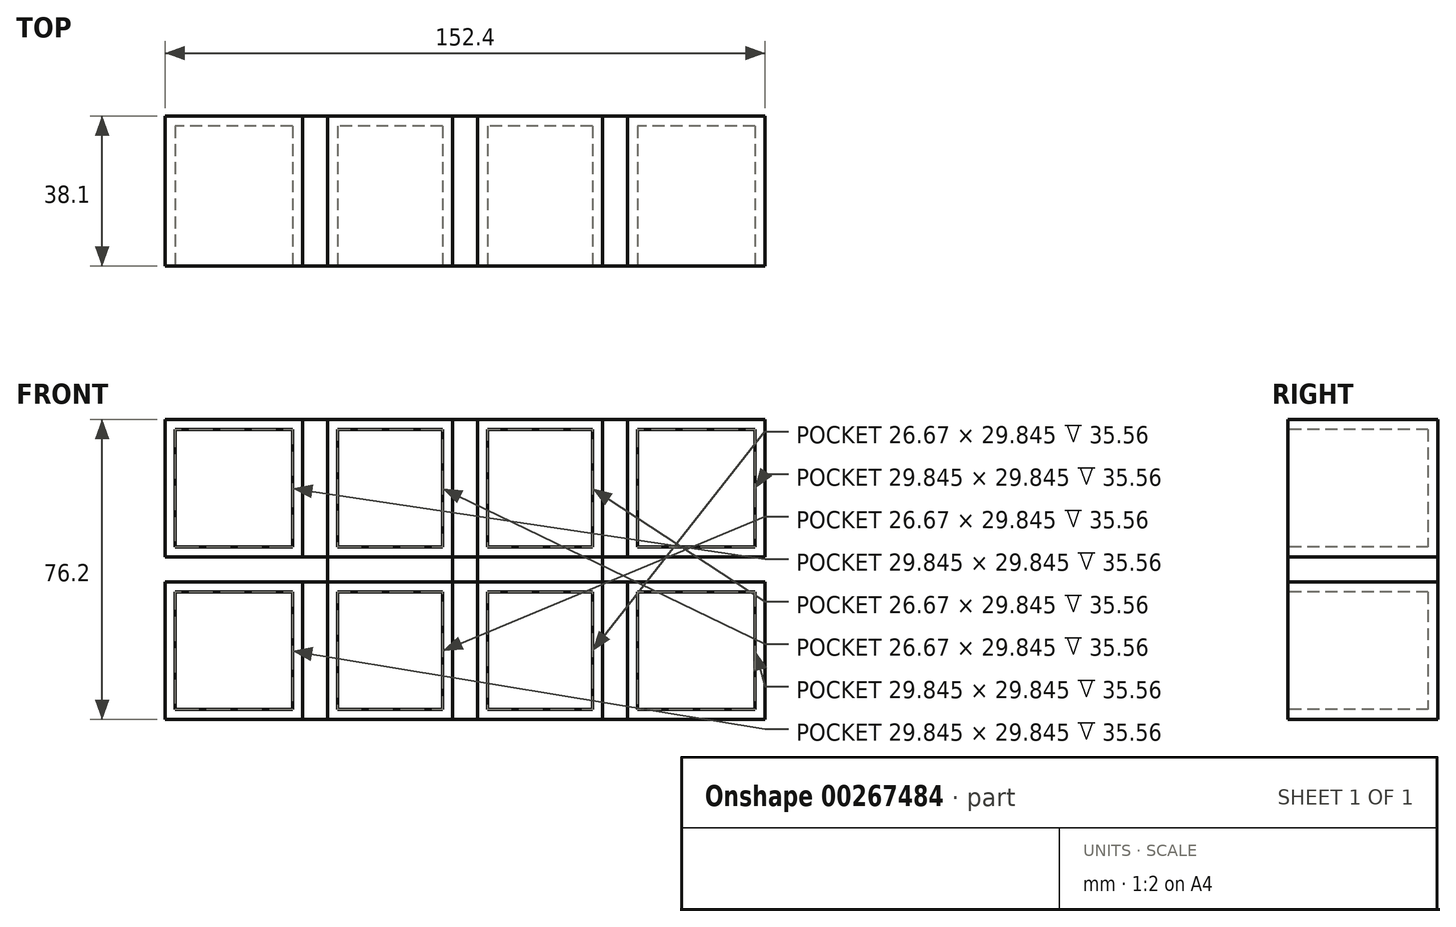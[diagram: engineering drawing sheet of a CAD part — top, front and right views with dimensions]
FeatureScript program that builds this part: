
annotation { "Feature Type Name" : "Feature", "Feature Type Description" : "" }
export const myFeature = defineFeature(function(context is Context, id is Id, definition is map)
    precondition{}
    {
        {
            var Q0;
            Q0=qCreatedBy(makeId("Front.planeOp"),FACE);
            var sketch = newSketch(context, id + "F0", { "sketchPlane" : qUnion([Q0])});
            skLineSegment(sketch, "E0.bottom", {"start": v(76.2, 38.1) * mm, "end": v(-76.2, 38.1) * mm});
            skLineSegment(sketch, "E0.top", {"start": v(76.2, -38.1) * mm, "end": v(-76.2, -38.1) * mm});
            skLineSegment(sketch, "E0.left", {"start": v(76.2, 38.1) * mm, "end": v(76.2, -38.1) * mm});
            skLineSegment(sketch, "E0.right", {"start": v(-76.2, 38.1) * mm, "end": v(-76.2, -38.1) * mm});
            skPoint(sketch, "E0.middle", {"position": v(0, 0) * mm});
            skLineSegment(sketch, "E1.bottom", {"start": v(76.2, -3.18) * mm, "end": v(-76.2, -3.18) * mm});
            skLineSegment(sketch, "E1.top", {"start": v(76.2, 3.18) * mm, "end": v(-76.2, 3.18) * mm});
            skLineSegment(sketch, "E1.left", {"start": v(76.2, -3.18) * mm, "end": v(76.2, 3.18) * mm});
            skLineSegment(sketch, "E1.right", {"start": v(-76.2, -3.18) * mm, "end": v(-76.2, 3.18) * mm});
            skLineSegment(sketch, "E2.bottom", {"start": v(-3.18, 38.1) * mm, "end": v(3.18, 38.1) * mm});
            skLineSegment(sketch, "E2.top", {"start": v(-3.18, -38.1) * mm, "end": v(3.18, -38.1) * mm});
            skLineSegment(sketch, "E2.left", {"start": v(-3.18, 38.1) * mm, "end": v(-3.18, -38.1) * mm});
            skLineSegment(sketch, "E2.right", {"start": v(3.18, 38.1) * mm, "end": v(3.18, -38.1) * mm});
            skLineSegment(sketch, "E3.bottom", {"start": v(38.1, -38.1) * mm, "end": v(-38.1, -38.1) * mm});
            skLineSegment(sketch, "E3.top", {"start": v(38.1, 38.1) * mm, "end": v(-38.1, 38.1) * mm});
            skLineSegment(sketch, "E4.bottom", {"start": v(-34.93, 38.1) * mm, "end": v(-41.28, 38.1) * mm});
            skLineSegment(sketch, "E4.top", {"start": v(-34.92, -38.1) * mm, "end": v(-41.27, -38.1) * mm});
            skLineSegment(sketch, "E4.left", {"start": v(-34.93, 38.1) * mm, "end": v(-34.93, -38.1) * mm});
            skLineSegment(sketch, "E4.right", {"start": v(-41.28, 38.1) * mm, "end": v(-41.28, -38.1) * mm});
            skPoint(sketch, "E4.middle", {"position": v(-38.1, 0) * mm});
            skLineSegment(sketch, "E5.bottom", {"start": v(41.28, 38.1) * mm, "end": v(34.93, 38.1) * mm});
            skLineSegment(sketch, "E5.top", {"start": v(41.28, -38.1) * mm, "end": v(34.93, -38.1) * mm});
            skLineSegment(sketch, "E5.left", {"start": v(41.28, 38.1) * mm, "end": v(41.28, -38.1) * mm});
            skLineSegment(sketch, "E5.right", {"start": v(34.92, 38.1) * mm, "end": v(34.92, -38.1) * mm});
            skPoint(sketch, "E5.middle", {"position": v(38.1, 0) * mm});
            skSolve(sketch);
        }
        {
            var Q0;
            {var subQ0=sQuery(id+"F0.wireOp",EDGE,"E0.right");var subQ1=sQuery(id+"F0.wireOp",EDGE,"E0.bottom");var subQ2=makeQuery(id+"F0.imprint","INTERSECT",VERTEX,{"derivedFrom":[subQ1,subQ0]});Q0=makeQuery(id+"F0.imprint","IMPRINT",FACE,{"disambiguationData":[TD([[makeQuery(id+"F0.imprint","IMPRINT",EDGE,{"disambiguationData":[TD([[subQ2,1.0]])],"derivedFrom":subQ1}),1.0]])]});}
            var Q1;
            {var subQ0=sQuery(id+"F0.wireOp",EDGE,"E2.left");var subQ1=sQuery(id+"F0.wireOp",EDGE,"E1.top");var subQ2=makeQuery(id+"F0.imprint","INTERSECT",VERTEX,{"derivedFrom":[subQ1,subQ0]});Q1=makeQuery(id+"F0.imprint","IMPRINT",FACE,{"disambiguationData":[TD([[makeQuery(id+"F0.imprint","IMPRINT",EDGE,{"disambiguationData":[TD([[subQ2,-1.0]])],"derivedFrom":subQ1}),-1.0]])]});}
            var Q2;
            {var subQ0=sQuery(id+"F0.wireOp",EDGE,"E5.right");var subQ1=sQuery(id+"F0.wireOp",EDGE,"E1.top");var subQ2=makeQuery(id+"F0.imprint","INTERSECT",VERTEX,{"derivedFrom":[subQ1,subQ0]});Q2=makeQuery(id+"F0.imprint","IMPRINT",FACE,{"disambiguationData":[TD([[makeQuery(id+"F0.imprint","IMPRINT",EDGE,{"disambiguationData":[TD([[subQ2,-1.0]])],"derivedFrom":subQ1}),-1.0]])]});}
            var Q3;
            {var subQ0=sQuery(id+"F0.wireOp",EDGE,"E0.left");var subQ1=sQuery(id+"F0.wireOp",EDGE,"E0.bottom");var subQ2=makeQuery(id+"F0.imprint","INTERSECT",VERTEX,{"derivedFrom":[subQ1,subQ0]});Q3=makeQuery(id+"F0.imprint","IMPRINT",FACE,{"disambiguationData":[TD([[makeQuery(id+"F0.imprint","IMPRINT",EDGE,{"disambiguationData":[TD([[subQ2,-1.0]])],"derivedFrom":subQ1}),1.0]])]});}
            var Q4;
            {var subQ0=sQuery(id+"F0.wireOp",EDGE,"E0.left");var subQ1=sQuery(id+"F0.wireOp",EDGE,"E0.top");var subQ2=makeQuery(id+"F0.imprint","INTERSECT",VERTEX,{"derivedFrom":[subQ1,subQ0]});Q4=makeQuery(id+"F0.imprint","IMPRINT",FACE,{"disambiguationData":[TD([[makeQuery(id+"F0.imprint","IMPRINT",EDGE,{"disambiguationData":[TD([[subQ2,-1.0]])],"derivedFrom":subQ1}),-1.0]])]});}
            var Q5;
            {var subQ0=sQuery(id+"F0.wireOp",EDGE,"E5.right");var subQ1=sQuery(id+"F0.wireOp",EDGE,"E1.bottom");var subQ2=makeQuery(id+"F0.imprint","INTERSECT",VERTEX,{"derivedFrom":[subQ1,subQ0]});Q5=makeQuery(id+"F0.imprint","IMPRINT",FACE,{"disambiguationData":[TD([[makeQuery(id+"F0.imprint","IMPRINT",EDGE,{"disambiguationData":[TD([[subQ2,-1.0]])],"derivedFrom":subQ1}),1.0]])]});}
            var Q6;
            {var subQ0=sQuery(id+"F0.wireOp",EDGE,"E2.left");var subQ1=sQuery(id+"F0.wireOp",EDGE,"E1.bottom");var subQ2=makeQuery(id+"F0.imprint","INTERSECT",VERTEX,{"derivedFrom":[subQ1,subQ0]});Q6=makeQuery(id+"F0.imprint","IMPRINT",FACE,{"disambiguationData":[TD([[makeQuery(id+"F0.imprint","IMPRINT",EDGE,{"disambiguationData":[TD([[subQ2,-1.0]])],"derivedFrom":subQ1}),1.0]])]});}
            var Q7;
            {var subQ0=sQuery(id+"F0.wireOp",EDGE,"E0.right");var subQ1=sQuery(id+"F0.wireOp",EDGE,"E0.top");var subQ2=makeQuery(id+"F0.imprint","INTERSECT",VERTEX,{"derivedFrom":[subQ1,subQ0]});Q7=makeQuery(id+"F0.imprint","IMPRINT",FACE,{"disambiguationData":[TD([[makeQuery(id+"F0.imprint","IMPRINT",EDGE,{"disambiguationData":[TD([[subQ2,1.0]])],"derivedFrom":subQ1}),-1.0]])]});}
            extrude(context, id + "F1", {"entities" : qUnion([Q0, Q1, Q2, Q3, Q4, Q5, Q6, Q7]), "oppositeDirection" : true, "depth" : 38.1 * mm});
        }
        {
            var Q0;
            Q0=makeQuery(id+"F1.opExtrude","CAP_FACE",FACE,{"disambiguationData":[OSD([sQuery(id+"F0.wireOp",EDGE,"E0.bottom"),sQuery(id+"F0.wireOp",EDGE,"E0.right"),sQuery(id+"F0.wireOp",EDGE,"E1.top"),sQuery(id+"F0.wireOp",EDGE,"E4.right")])],"isStart":true});
            var Q1;
            Q1=makeQuery(id+"F1.opExtrude","CAP_FACE",FACE,{"disambiguationData":[OSD([sQuery(id+"F0.wireOp",EDGE,"E1.top"),sQuery(id+"F0.wireOp",EDGE,"E2.left"),sQuery(id+"F0.wireOp",EDGE,"E3.top"),sQuery(id+"F0.wireOp",EDGE,"E4.left")])],"isStart":true});
            var Q2;
            Q2=makeQuery(id+"F1.opExtrude","CAP_FACE",FACE,{"disambiguationData":[OSD([sQuery(id+"F0.wireOp",EDGE,"E1.top"),sQuery(id+"F0.wireOp",EDGE,"E2.right"),sQuery(id+"F0.wireOp",EDGE,"E3.top"),sQuery(id+"F0.wireOp",EDGE,"E5.right")])],"isStart":true});
            var Q3;
            Q3=makeQuery(id+"F1.opExtrude","CAP_FACE",FACE,{"disambiguationData":[OSD([sQuery(id+"F0.wireOp",EDGE,"E0.bottom"),sQuery(id+"F0.wireOp",EDGE,"E0.left"),sQuery(id+"F0.wireOp",EDGE,"E1.top"),sQuery(id+"F0.wireOp",EDGE,"E5.left")])],"isStart":true});
            var Q4;
            Q4=makeQuery(id+"F1.opExtrude","CAP_FACE",FACE,{"disambiguationData":[OSD([sQuery(id+"F0.wireOp",EDGE,"E0.top"),sQuery(id+"F0.wireOp",EDGE,"E0.left"),sQuery(id+"F0.wireOp",EDGE,"E1.bottom"),sQuery(id+"F0.wireOp",EDGE,"E5.left")])],"isStart":true});
            var Q5;
            Q5=makeQuery(id+"F1.opExtrude","CAP_FACE",FACE,{"disambiguationData":[OSD([sQuery(id+"F0.wireOp",EDGE,"E1.bottom"),sQuery(id+"F0.wireOp",EDGE,"E2.right"),sQuery(id+"F0.wireOp",EDGE,"E3.bottom"),sQuery(id+"F0.wireOp",EDGE,"E5.right")])],"isStart":true});
            var Q6;
            Q6=makeQuery(id+"F1.opExtrude","CAP_FACE",FACE,{"disambiguationData":[OSD([sQuery(id+"F0.wireOp",EDGE,"E1.bottom"),sQuery(id+"F0.wireOp",EDGE,"E2.left"),sQuery(id+"F0.wireOp",EDGE,"E3.bottom"),sQuery(id+"F0.wireOp",EDGE,"E4.left")])],"isStart":true});
            var Q7;
            Q7=makeQuery(id+"F1.opExtrude","CAP_FACE",FACE,{"disambiguationData":[OSD([sQuery(id+"F0.wireOp",EDGE,"E0.top"),sQuery(id+"F0.wireOp",EDGE,"E0.right"),sQuery(id+"F0.wireOp",EDGE,"E1.bottom"),sQuery(id+"F0.wireOp",EDGE,"E4.right")])],"isStart":true});
            shell(context, id + "F2", {"entities" : qUnion([Q0, Q1, Q2, Q3, Q4, Q5, Q6, Q7]), "thickness" : 2.54 * mm});
        }
        {
            var Q0;
            {var subQ0=sQuery(id+"F0.wireOp",EDGE,"E1.right");Q0=makeQuery(id+"F0.imprint","IMPRINT",FACE,{"disambiguationData":[TD([[makeQuery(id+"F0.imprint","IMPRINT",EDGE,{"derivedFrom":subQ0}),-1.0]])]});}
            var Q1;
            {var subQ0=sQuery(id+"F0.wireOp",EDGE,"E4.left");var subQ1=sQuery(id+"F0.wireOp",EDGE,"E1.top");var subQ2=makeQuery(id+"F0.imprint","INTERSECT",VERTEX,{"derivedFrom":[subQ1,subQ0]});Q1=makeQuery(id+"F0.imprint","IMPRINT",FACE,{"disambiguationData":[TD([[makeQuery(id+"F0.imprint","IMPRINT",EDGE,{"disambiguationData":[TD([[subQ2,-1.0]])],"derivedFrom":subQ1}),-1.0]])]});}
            var Q2;
            {var subQ0=sQuery(id+"F0.wireOp",EDGE,"E2.left");var subQ1=sQuery(id+"F0.wireOp",EDGE,"E1.bottom");var subQ2=makeQuery(id+"F0.imprint","INTERSECT",VERTEX,{"derivedFrom":[subQ1,subQ0]});Q2=makeQuery(id+"F0.imprint","IMPRINT",FACE,{"disambiguationData":[TD([[makeQuery(id+"F0.imprint","IMPRINT",EDGE,{"disambiguationData":[TD([[subQ2,-1.0]])],"derivedFrom":subQ1}),-1.0]])]});}
            var Q3;
            {var subQ0=sQuery(id+"F0.wireOp",EDGE,"E4.left");var subQ1=sQuery(id+"F0.wireOp",EDGE,"E1.bottom");var subQ2=makeQuery(id+"F0.imprint","INTERSECT",VERTEX,{"derivedFrom":[subQ1,subQ0]});Q3=makeQuery(id+"F0.imprint","IMPRINT",FACE,{"disambiguationData":[TD([[makeQuery(id+"F0.imprint","IMPRINT",EDGE,{"disambiguationData":[TD([[subQ2,-1.0]])],"derivedFrom":subQ1}),1.0]])]});}
            var Q4;
            {var subQ0=sQuery(id+"F0.wireOp",EDGE,"E2.right");var subQ1=sQuery(id+"F0.wireOp",EDGE,"E1.bottom");var subQ2=makeQuery(id+"F0.imprint","INTERSECT",VERTEX,{"derivedFrom":[subQ1,subQ0]});Q4=makeQuery(id+"F0.imprint","IMPRINT",FACE,{"disambiguationData":[TD([[makeQuery(id+"F0.imprint","IMPRINT",EDGE,{"disambiguationData":[TD([[subQ2,-1.0]])],"derivedFrom":subQ1}),1.0]])]});}
            var Q5;
            {var subQ0=sQuery(id+"F0.wireOp",EDGE,"E2.right");var subQ1=sQuery(id+"F0.wireOp",EDGE,"E1.top");var subQ2=makeQuery(id+"F0.imprint","INTERSECT",VERTEX,{"derivedFrom":[subQ1,subQ0]});Q5=makeQuery(id+"F0.imprint","IMPRINT",FACE,{"disambiguationData":[TD([[makeQuery(id+"F0.imprint","IMPRINT",EDGE,{"disambiguationData":[TD([[subQ2,-1.0]])],"derivedFrom":subQ1}),-1.0]])]});}
            var Q6;
            {var subQ0=sQuery(id+"F0.wireOp",EDGE,"E5.left");var subQ1=sQuery(id+"F0.wireOp",EDGE,"E1.top");var subQ2=makeQuery(id+"F0.imprint","INTERSECT",VERTEX,{"derivedFrom":[subQ1,subQ0]});Q6=makeQuery(id+"F0.imprint","IMPRINT",FACE,{"disambiguationData":[TD([[makeQuery(id+"F0.imprint","IMPRINT",EDGE,{"disambiguationData":[TD([[subQ2,-1.0]])],"derivedFrom":subQ1}),-1.0]])]});}
            var Q7;
            {var subQ0=sQuery(id+"F0.wireOp",EDGE,"E5.left");var subQ1=sQuery(id+"F0.wireOp",EDGE,"E1.bottom");var subQ2=makeQuery(id+"F0.imprint","INTERSECT",VERTEX,{"derivedFrom":[subQ1,subQ0]});Q7=makeQuery(id+"F0.imprint","IMPRINT",FACE,{"disambiguationData":[TD([[makeQuery(id+"F0.imprint","IMPRINT",EDGE,{"disambiguationData":[TD([[subQ2,-1.0]])],"derivedFrom":subQ1}),1.0]])]});}
            var Q8;
            {var subQ0=sQuery(id+"F0.wireOp",EDGE,"E1.left");Q8=makeQuery(id+"F0.imprint","IMPRINT",FACE,{"disambiguationData":[TD([[makeQuery(id+"F0.imprint","IMPRINT",EDGE,{"derivedFrom":subQ0}),1.0]])]});}
            var Q9;
            {var subQ0=sQuery(id+"F0.wireOp",EDGE,"E5.right");var subQ1=sQuery(id+"F0.wireOp",EDGE,"E1.bottom");var subQ2=makeQuery(id+"F0.imprint","INTERSECT",VERTEX,{"derivedFrom":[subQ1,subQ0]});Q9=makeQuery(id+"F0.imprint","IMPRINT",FACE,{"disambiguationData":[TD([[makeQuery(id+"F0.imprint","IMPRINT",EDGE,{"disambiguationData":[TD([[subQ2,-1.0]])],"derivedFrom":subQ1}),-1.0]])]});}
            extrude(context, id + "F3", {"entities" : qUnion([Q0, Q1, Q2, Q3, Q4, Q5, Q6, Q7, Q8, Q9]), "oppositeDirection" : true, "depth" : 38.1 * mm});
        }
    });
